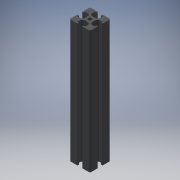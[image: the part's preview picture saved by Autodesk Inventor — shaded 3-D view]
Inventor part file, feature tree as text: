
AUTODESK INVENTOR PART (.ipt)
format: ipt  version: 2016 (Build 200138000, 138)  size: 170,496 bytes
history: native  units: mm
features: extrude x1, sketch x1
ambient origin geometry x8: Origin, YZ Plane, XZ Plane, XY Plane, X Axis, Y Axis, Z Axis, Center Point
bodies: Solid1 (feature_tree)
feature tree (2):
  extrude  "Extrusion1"  [1 undecoded]
  sketch  "Sketch_1"  dims[d0=90.0mm d1=0.0mm]
note: 1 required parameter value undecoded (feature->parameter linkage not recoverable at this tier; creation-order binding heuristic only, values carry confidence <= 0.55)
